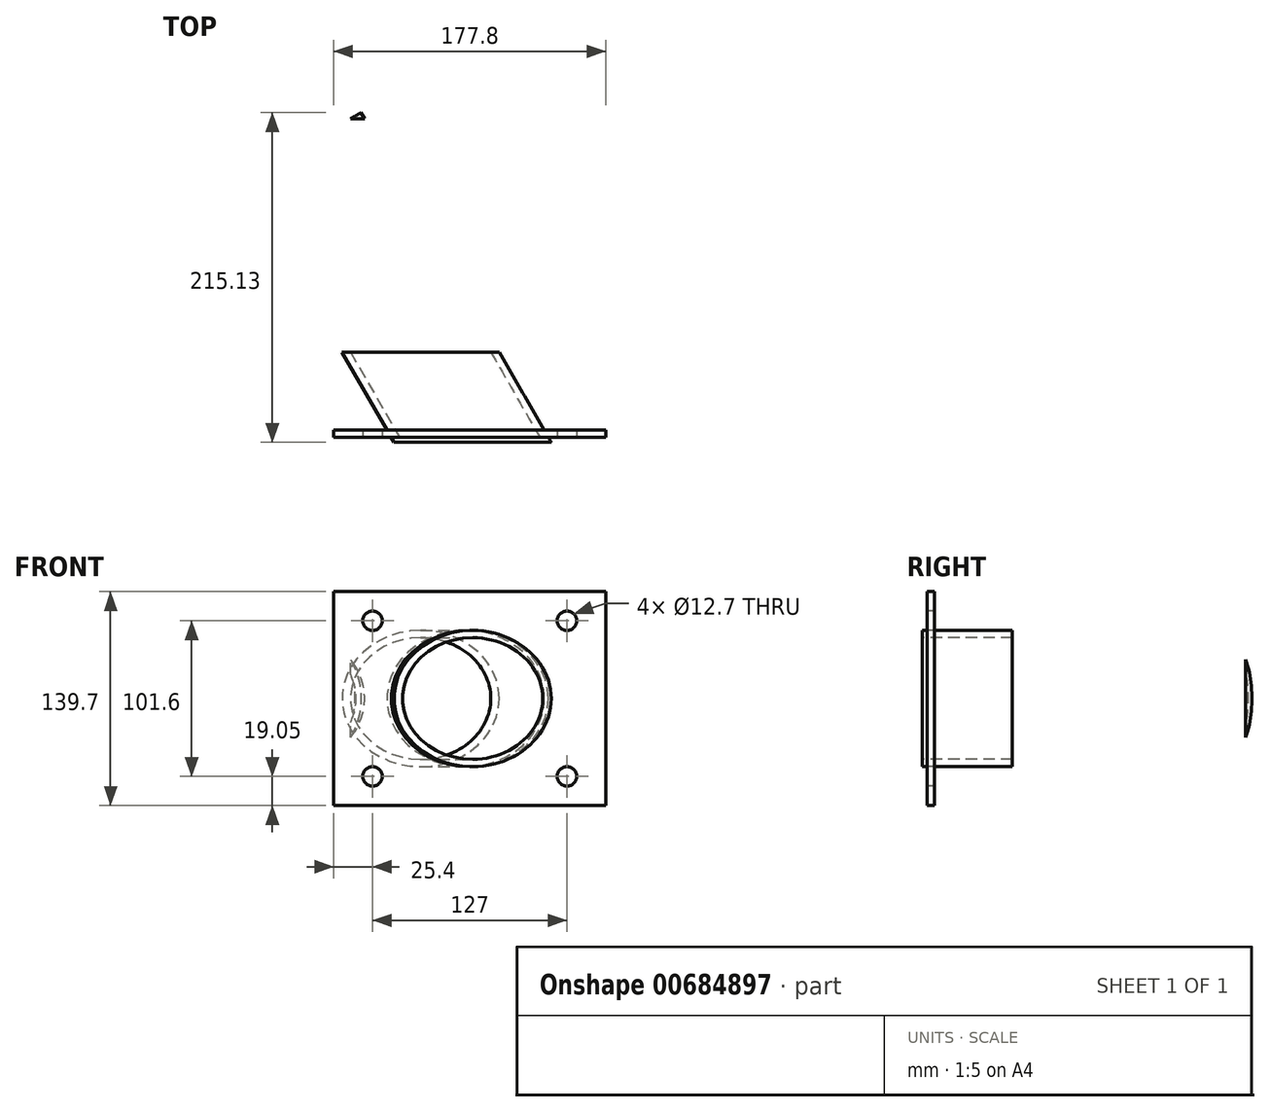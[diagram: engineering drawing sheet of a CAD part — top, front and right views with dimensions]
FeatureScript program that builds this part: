
annotation { "Feature Type Name" : "Feature", "Feature Type Description" : "" }
export const myFeature = defineFeature(function(context is Context, id is Id, definition is map)
    precondition{}
    {
        {
            var Q0;
            Q0=qCreatedBy(makeId("Front.planeOp"),FACE);
            var sketch = newSketch(context, id + "F0", { "sketchPlane" : qUnion([Q0])});
            skLineSegment(sketch, "E0.bottom", {"start": v(88.9, 69.85) * mm, "end": v(-88.9, 69.85) * mm});
            skLineSegment(sketch, "E0.top", {"start": v(88.9, -69.85) * mm, "end": v(-88.9, -69.85) * mm});
            skLineSegment(sketch, "E0.left", {"start": v(88.9, 69.85) * mm, "end": v(88.9, -69.85) * mm});
            skLineSegment(sketch, "E0.right", {"start": v(-88.9, 69.85) * mm, "end": v(-88.9, -69.85) * mm});
            skPoint(sketch, "E0.middle", {"position": v(0, 0) * mm});
            skSolve(sketch);
        }
        {
            var Q0;
            Q0 = qSketchRegion(id + "F0", true);
            extrude(context, id + "F1", {"entities" : qUnion([Q0]), "oppositeDirection" : true, "depth" : 4.76 * mm, "offsetDistance" : 25.4 * mm});
        }
        {
            var Q0;
            Q0=qCreatedBy(makeId("Top.planeOp"),FACE);
            var sketch = newSketch(context, id + "F2", { "sketchPlane" : qUnion([Q0])});
            skLineSegment(sketch, "E1", {"start": v(-37, -61.69) * mm, "end": v(69.85, 0) * mm, "construction": true});
            skSolve(sketch);
        }
        {
            var Q0;
            Q0=sQuery(id+"F2.wireOp",EDGE,"E1");
            var Q1;
            Q1=qCreatedBy(makeId("Front.planeOp"),FACE);
            cPlane(context, id + "F3", {"entities" : qUnion([Q0, Q1]), "cplaneType" : CPlaneType.LINE_ANGLE, "offset" : 25.4 * mm, "angle" : 0 * degree, "width" : 152.4 * mm, "height" : 152.4 * mm});
        }
        {
            var Q0;
            Q0=qCreatedBy(id+"F3.planeOp",FACE);
            var sketch = newSketch(context, id + "F4", { "sketchPlane" : qUnion([Q0])});
            skCircle(sketch, "E2", {"center": v(0, 0) * mm, "radius": 44.45 * mm});
            skSolve(sketch);
        }
        {
            var Q0;
            Q0 = qSketchRegion(id + "F4", true);
            extrude(context, id + "F5", {"entities" : qUnion([Q0]), "operationType" : NewBodyOperationType.ADD, "depth" : 254 * mm, "offsetDistance" : 25.4 * mm});
        }
        {
            var Q0;
            Q0=qCreatedBy(id+"F3.planeOp",FACE);
            var sketch = newSketch(context, id + "F6", { "sketchPlane" : qUnion([Q0])});
            skCircle(sketch, "E3", {"center": v(0, 0) * mm, "radius": 39.69 * mm});
            skSolve(sketch);
        }
        {
            var Q0;
            Q0 = qSketchRegion(id + "F6", true);
            extrude(context, id + "F7", {"entities" : qUnion([Q0]), "operationType" : NewBodyOperationType.REMOVE, "endBound" : BoundingType.THROUGH_ALL, "depth" : 25.4 * mm, "offsetDistance" : 25.4 * mm});
        }
        {
            var Q0;
            Q0=qCreatedBy(makeId("Top.planeOp"),FACE);
            var sketch = newSketch(context, id + "F8", { "sketchPlane" : qUnion([Q0])});
            skLineSegment(sketch, "E4.bottom", {"start": v(-88.9, -3.18) * mm, "end": v(88.9, -3.18) * mm});
            skLineSegment(sketch, "E4.top", {"start": v(-88.9, -79.38) * mm, "end": v(88.9, -79.38) * mm});
            skLineSegment(sketch, "E4.left", {"start": v(-88.9, -3.18) * mm, "end": v(-88.9, -79.38) * mm});
            skLineSegment(sketch, "E4.right", {"start": v(88.9, -3.18) * mm, "end": v(88.9, -79.38) * mm});
            skSolve(sketch);
        }
        {
            var Q0;
            Q0 = qSketchRegion(id + "F8", true);
            var Q1;
            {var subQ0=sQuery(id+"F4.wireOp",EDGE,"E2");Q1=makeQuery(id+"F5.boolean.opBoolean","SPLIT",FACE,{"disambiguationData":[TD([makeQuery(id+"F5.opExtrude","CAP_FACE",FACE,{"disambiguationData":[OSD([subQ0,sQuery(id+"F4.wireOp",EDGE,"ZPCoHywG-Gp1d-M8Lw-pocQ-Q5KS3TjvjPmC")])],"isStart":true})])],"derivedFrom":makeQuery(id+"F5.opExtrude","SWEPT_FACE",FACE,{"disambiguationData":[OSD([subQ0])]})});}
            extrude(context, id + "F9", {"entities" : qUnion([Q0]), "operationType" : NewBodyOperationType.REMOVE, "oppositeDirection" : true, "depth" : 101.6 * mm, "endBoundEntityFace" : qUnion([Q1]), "offsetDistance" : 25.4 * mm, "hasSecondDirection" : true, "secondDirectionBound" : BoundingType.UP_TO_SURFACE, "secondDirectionOppositeDirection" : false, "secondDirectionDepth" : 25.4 * mm, "symmetric" : true});
        }
        {
            var Q0;
            Q0=makeQuery(id+"F1.opExtrude","CAP_FACE",FACE,{"disambiguationData":[OSD([sQuery(id+"F0.wireOp",EDGE,"E0.bottom"),sQuery(id+"F0.wireOp",EDGE,"E0.top"),sQuery(id+"F0.wireOp",EDGE,"E0.left"),sQuery(id+"F0.wireOp",EDGE,"E0.right")])],"isStart":true});
            var sketch = newSketch(context, id + "F10", { "sketchPlane" : qUnion([Q0])});
            skLineSegment(sketch, "E5", {"start": v(-193.59, 0) * mm, "end": v(261.76, 0) * mm, "construction": true});
            skLineSegment(sketch, "E6", {"start": v(0, 196.6) * mm, "end": v(0, -220.88) * mm, "construction": true});
            skLineSegment(sketch, "E7", {"start": v(-193.59, 50.8) * mm, "end": v(230.79, 50.8) * mm, "construction": true});
            skLineSegment(sketch, "E8", {"start": v(-63.5, 176.56) * mm, "end": v(-63.5, -155.34) * mm, "construction": true});
            skCircle(sketch, "E9", {"center": v(-63.5, 50.8) * mm, "radius": 6.35 * mm});
            skCircle(sketch, "E10.MirrorC", {"center": v(63.5, 50.8) * mm, "radius": 6.35 * mm});
            skLineSegment(sketch, "E11.MirrorCS", {"start": v(193.59, 0) * mm, "end": v(-261.76, 0) * mm, "construction": true});
            skCircle(sketch, "E12.MirrorC", {"center": v(-63.5, -50.8) * mm, "radius": 6.35 * mm});
            skCircle(sketch, "E13.MirrorC", {"center": v(63.5, -50.8) * mm, "radius": 6.35 * mm});
            skSolve(sketch);
        }
        {
            var Q0;
            Q0 = qSketchRegion(id + "F10", true);
            extrude(context, id + "F11", {"entities" : qUnion([Q0]), "operationType" : NewBodyOperationType.REMOVE, "endBound" : BoundingType.THROUGH_ALL, "oppositeDirection" : true, "depth" : 25.4 * mm, "offsetDistance" : 25.4 * mm});
        }
        {
            var Q0;
            Q0=qCreatedBy(makeId("Top.planeOp"),FACE);
            var sketch = newSketch(context, id + "F12", { "sketchPlane" : qUnion([Q0])});
            skLineSegment(sketch, "E14.bottom", {"start": v(-177.8, 207.96) * mm, "end": v(88.9, 207.96) * mm});
            skLineSegment(sketch, "E14.top", {"start": v(-177.8, 55.56) * mm, "end": v(88.9, 55.56) * mm});
            skLineSegment(sketch, "E14.left", {"start": v(-177.8, 207.96) * mm, "end": v(-177.8, 55.56) * mm});
            skLineSegment(sketch, "E14.right", {"start": v(88.9, 207.96) * mm, "end": v(88.9, 55.56) * mm});
            skSolve(sketch);
        }
        {
            var Q0;
            Q0 = qSketchRegion(id + "F12", true);
            extrude(context, id + "F13", {"entities" : qUnion([Q0]), "operationType" : NewBodyOperationType.REMOVE, "oppositeDirection" : true, "depth" : 88.9 * mm, "offsetDistance" : 25.4 * mm, "symmetric" : true});
        }
    });
